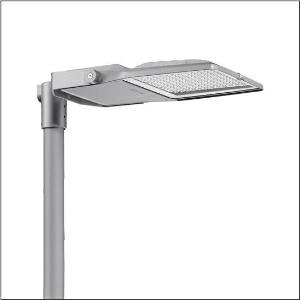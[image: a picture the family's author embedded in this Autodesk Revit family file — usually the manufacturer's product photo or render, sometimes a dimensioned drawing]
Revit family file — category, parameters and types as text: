
# Revit family: floodlight_fl_21_iq_midi___pl61_5xa7782e2c3a_85c4
name_source: partatom
category: Lighting Fixtures
units: mm (PartAtom-declared; Revit-internal decimal feet)

## family parameters
Cut with Voids When Loaded = No
Host = Face
Light Source = No
Part Type = Normal
Room Calculation Point = No
Round Connector Dimension = Use Diameter
Shared = No

## types (1)
- --- (1 x LED, 26360 lm, 208.1 W, 3000K)
    Apparent Load = 208 VA
    CIE Flux Codes = 33 65 98 100 100
    Color Rendering = 70
    Color Temperature = 3000K
    Default Elevation = 1800 mm
    Description = Floodlight FL 21 iQ midi, floodlight, primary light control with lens, of PMMA, primary optical cover: protective disc, of toughened safety glass, transparent, light distribution: PL61, light emission: direct distribution, installation type: surface-mounted, LED, High Power LED, rated luminous flux: 26.360lm, luminous efficacy: 127lm/W, light colour: 730, colour temperature: 3000K, control gear: ECG iQ, control: optimised constant luminous flux control (CLO 2.0), Desk-Remote (wireless, voltage-free reading and setting of iQ features in the workshop via application-optimized NFC function/RFID function), Smart-Wire, Night-Set, Temp-Guard, Auto-Match, Street-Remote, with terminal, 6-pole, mains connection: 220..240V, AC, 50/60Hz, start of lifetime: 208W, end of service life: 227W, reduction: 90W, luminaire housing, of diecast aluminium, powder-coated, Siteco® metallic grey (DB 702S), corrosivity category C5 mid according to DIN EN ISO 12944, sealing non-destructively replaceable, please order mast flange separately, mast bracket, of steel, galvanised, powder-coated, Siteco® metallic grey (DB 702S), protection rating (complete): IP66, insulation class (complete): insulation class II (safety insulation), certification: CE, ENEC, VDE, protection symbol: D, impact resistance: IK08, permissible operating ambient temperature: -40..+40°C, permissible operating ambient temperature for outdoor applications: -40..+50°C, standard: DIN EN 12944, LABS conformity tested according to VDMA 24364:2018-05, packaging unit: 1 piece

Light Distribution: PL61
    Height = 76 mm
    Lamp = 1 x LED
    Lamp Light Flux = 26360 lm
    Lamp Power = 208.1 W
    Lamp count = 1
    Length = 657 mm
    Luminous efficacy = 127 lm/W
    Manufacturer = Siteco
    ModVariant = No
    Model = 5XA7782E2C3A
    Number of Poles = 1
    OnlyDefault = Yes
    Power Factor = 1
    Product Name = Floodlight FL 21 iQ midi | PL61
    Product group = floodlight | pylon annexe
    ProductGroupID = 6200
    Protection Class = Protection class II
    Protection Degree = IP 66
    RLX_Detail_Level = 1
    RLX_Emergency_Light_Flux = 0 lm
    RLX_Emergency_Type = 0
    RLX_Emergency_Type_DB = No
    RlxData = <blob elided: 153677 chars, md5=4c0830b1>
    Socket = socket
    Standby Power = 0 W
    System Light Flux = 26360 lm
    System Power = 208 W
    Type Comments = factory setting: luminous flux: 100 % | dim-lin: 254 | 710 mA
    Type Image = l_1007123.jpg
    URL = http://relux.com
    VarID = @adj_077595
    Voltage = 0 V
    Weight = 0.00 kg
    Width = 442 mm

## geometry (parser evidence)
native form markers: Blend x4, Sweep x12
no freeform markers — native parametric forms only
